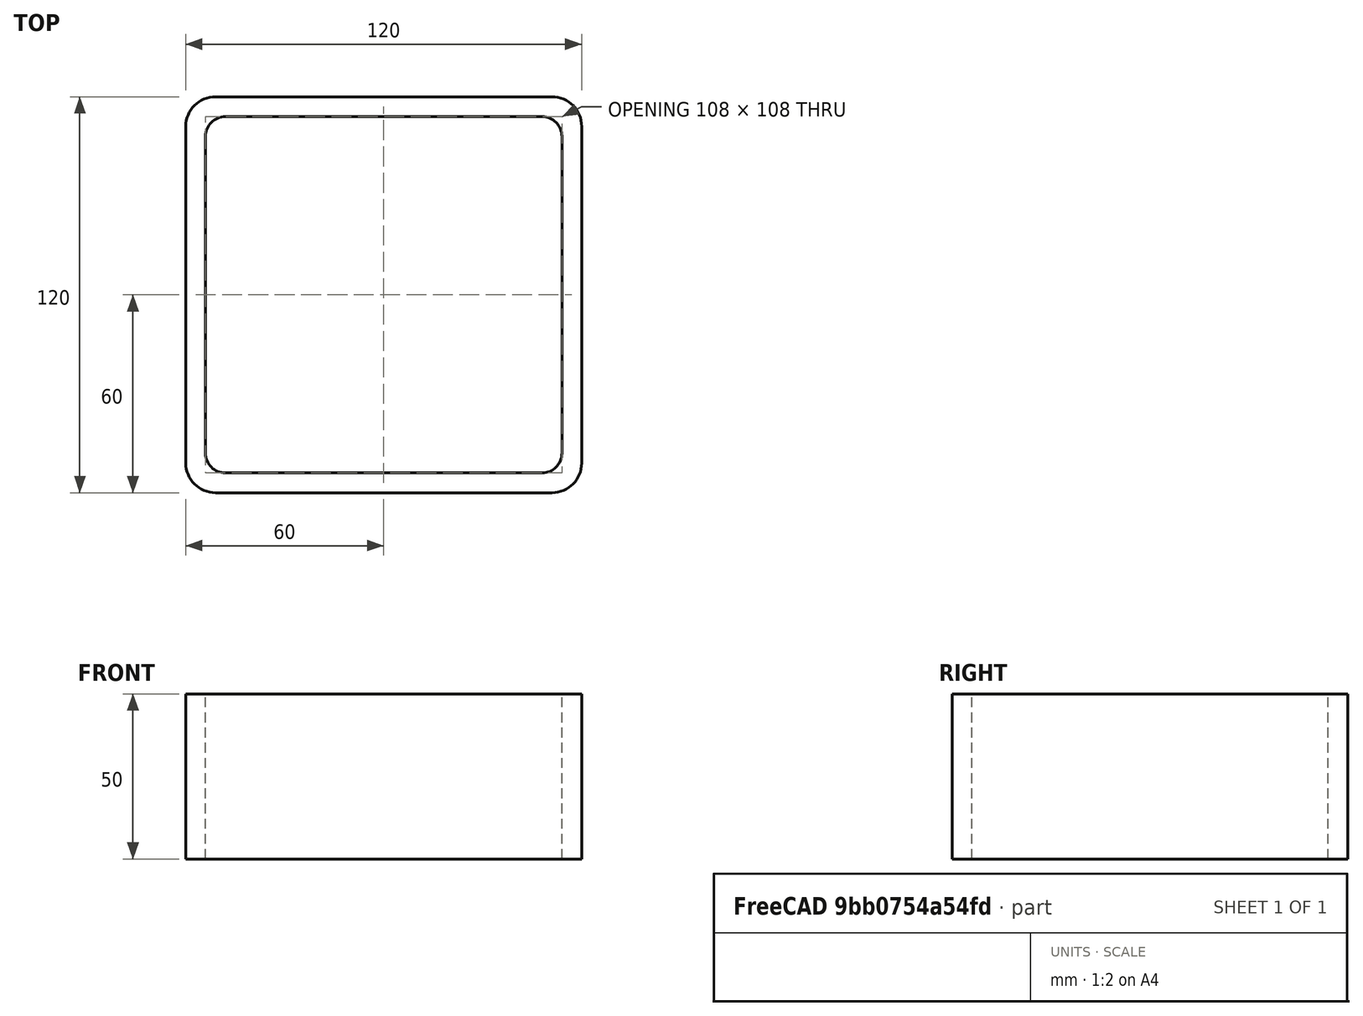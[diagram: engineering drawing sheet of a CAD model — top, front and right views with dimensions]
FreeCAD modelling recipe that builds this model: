
FCSTD DOCUMENT  (FreeCAD 0.15R4671 (Git))
Label: Square hollow section 120x120x6 EN10219 S235JRH
License: All rights reserved
LicenseURL: http://en.wikipedia.org/wiki/All_rights_reserved
objects: Sketcher::SketchObject×1, Part::Extrusion×1
note: 2 computed .brp shape members not serialized (recipe doc carries the construction recipe); baked Part::Feature solids carry a one-line shape summary decoded from their .brp

FEATURE [Sketcher::SketchObject] Sketch
  sketch-geometry (16):
    g0: LineSegment StartX=-48 StartY=54 StartZ=0 EndX=48 EndY=54 EndZ=0
    g1: LineSegment StartX=54 StartY=48 StartZ=0 EndX=54 EndY=-48 EndZ=0
    g2: LineSegment StartX=48 StartY=-54 StartZ=0 EndX=-48 EndY=-54 EndZ=0
    g3: LineSegment StartX=-54 StartY=-48 StartZ=0 EndX=-54 EndY=48 EndZ=0
    g4: LineSegment StartX=-51 StartY=60 StartZ=0 EndX=51 EndY=60 EndZ=0
    g5: LineSegment StartX=60 StartY=51 StartZ=0 EndX=60 EndY=-51 EndZ=0
    g6: LineSegment StartX=51 StartY=-60 StartZ=0 EndX=-51 EndY=-60 EndZ=0
    g7: LineSegment StartX=-60 StartY=-51 StartZ=0 EndX=-60 EndY=51 EndZ=0
    g8: ArcOfCircle CenterX=-48 CenterY=48 CenterZ=0 NormalX=0 NormalY=0 NormalZ=1 Radius=6 StartAngle=1.5708 EndAngle=3.14159
    g9: ArcOfCircle CenterX=48 CenterY=48 CenterZ=0 NormalX=0 NormalY=0 NormalZ=1 Radius=6 StartAngle=0 EndAngle=1.5708
    g10: ArcOfCircle CenterX=48 CenterY=-48 CenterZ=0 NormalX=0 NormalY=0 NormalZ=1 Radius=6 StartAngle=4.71239 EndAngle=6.28319
    g11: ArcOfCircle CenterX=-48 CenterY=-48 CenterZ=0 NormalX=0 NormalY=0 NormalZ=1 Radius=6 StartAngle=3.14159 EndAngle=4.71239
    g12: ArcOfCircle CenterX=51 CenterY=51 CenterZ=0 NormalX=0 NormalY=0 NormalZ=1 Radius=9 StartAngle=0 EndAngle=1.5708
    g13: ArcOfCircle CenterX=51 CenterY=-51 CenterZ=0 NormalX=0 NormalY=0 NormalZ=1 Radius=9 StartAngle=4.71239 EndAngle=6.28319
    g14: ArcOfCircle CenterX=-51 CenterY=-51 CenterZ=0 NormalX=0 NormalY=0 NormalZ=1 Radius=9 StartAngle=3.14159 EndAngle=4.71239
    g15: ArcOfCircle CenterX=-51 CenterY=51 CenterZ=0 NormalX=0 NormalY=0 NormalZ=1 Radius=9 StartAngle=1.5708 EndAngle=3.14159
  constraints (36):
    c: Horizontal(g2)
    c: Vertical(g3)
    c: Horizontal(g6)
    c: Vertical(g7)
    c: Tangent(g3,g8) = 1.5708
    c: Tangent(g0,g8) = 1.5708
    c: Tangent(g0,g9) = 1.5708
    c: Tangent(g1,g9) = 1.5708
    c: Tangent(g1,g10) = 1.5708
    c: Tangent(g2,g10) = 1.5708
    c: Tangent(g2,g11) = 1.5708
    c: Tangent(g3,g11) = 1.5708
    c: Tangent(g4,g12) = 1.5708
    c: Tangent(g5,g12) = 1.5708
    c: Tangent(g5,g13) = 1.5708
    c: Tangent(g6,g13) = 1.5708
    c: Tangent(g6,g14) = 1.5708
    c: Tangent(g7,g14) = 1.5708
    c: Tangent(g7,g15) = 1.5708
    c: Tangent(g4,g15) = 1.5708
    c: Equal(g9,g8)
    c: Equal(g9,g11)
    c: Equal(g9,g10)
    c: Equal(g12,g15)
    c: Equal(g12,g14)
    c: Equal(g12,g13)
    c: Symmetric(g4,g6,g-1)
    c: Symmetric(g7,g5,g-2)
    c: DistanceY(g4,g6) = -120
    c: DistanceX(g7,g5) = 120
    c: Symmetric(g3,g1,g-2)
    c: Symmetric(g0,g2,g-1)
    c: DistanceY(g0,g4) = 6
    c: DistanceX(g5,g1) = -6
    c: Radius(g9) = 6
    c: Radius(g12) = 9
FEATURE [Part::Extrusion] Extrude  label="Square hollow section 120x120x6 EN10219 S235JRH"
  Base = -> Sketch
  Dir = (0,0,50)
  Solid = true
